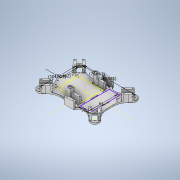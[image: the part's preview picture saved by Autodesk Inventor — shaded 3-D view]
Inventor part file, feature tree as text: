
AUTODESK INVENTOR PART (.ipt)
format: ipt  version: 2020.3 (Build 243373000, 373)  size: 1,453,056 bytes
history: native  units: mm
features: sketch x9, extrude x9, fillet x8, hole x7, projected_geometry x2, plane x1
ambient origin geometry x8: Origin, YZ Plane, XZ Plane, XY Plane, X Axis, Y Axis, Z Axis, Center Point
bodies: Body1 (feature_tree)
feature tree (36):
  sketch  "Sketch1"  dims[d0=135.0deg d4=24.6mm]
  extrude  "Extrusion10"  Depth=24.6mm
  extrude  "Extrusion11"  Depth=70.0mm
  extrude  "Extrusion12"  Depth=8.7mm
  sketch  "Sketch12"  dims[d53=1.5mm d54=20.0mm d59=1.0mm d60=90.0mm d61=135.0deg d70=135.0deg d82=0.7mm d83=0.7mm d84=0.7mm d85=0.7mm d86=6.0mm d87=5.0mm d88=0.0mm d89=20.92mm d90=0.0mm d91=1.9mm d92=6.0mm d93=4.2mm d94=2.0mm d95=90.0deg d96=8.0mm d97=0.0mm d98=2.0mm d99=1.0mm d100=2.0mm d101=0.5mm d103=0.5mm d104=0.5mm d105=18.0mm d108=3.0mm d110=2.9mm d111=6.0mm d112=4.0mm d113=2.0mm d114=90.0deg d115=4.3mm d116=0.0mm d117=30.0mm d119=84.0mm d120=1.9mm d121=6.0mm d122=4.0mm d123=2.0mm d124=90.0deg d125=8.0mm d126=0.0mm d128=12.0mm d129=2.094395mm d130=6.0mm d134=32.32mm d135=0.0mm d136=0.3mm d137=5.6mm d138=6.0mm d139=9.0mm d140=1.1mm d141=90.0deg d142=6.6mm d143=0.0mm d144=0.2mm d145=1.0mm d146=1.5mm d147=10.0mm d148=0.0mm d149=0.0mm d150=1.0mm d151=10.0mm d152=1.5mm d153=10.0mm d154=0.0mm d155=1.0mm d156=10.0mm d158=1.5mm d159=10.0mm d160=0.0mm d161=1.0mm d162=10.0mm d163=1.5mm d164=10.0mm d165=0.0mm d166=2.0mm d173=0.5mm d174=4.0mm d175=1.0mm d176=3.0mm d177=0.5mm d178=9.7mm d179=4.0mm d181=0.2mm d182=6.0mm d183=4.0mm d185=21.842mm d186=0.0mm d187=0.3mm d188=24.0mm d189=52.462385mm d190=74.962385mm d191=2.0mm d192=2.0mm d193=2.0mm d194=2.1mm d195=6.0mm d196=4.0mm d197=2.0mm d198=90.0deg d199=7.3mm d200=0.0mm d201=10.0mm d204=30.0deg d205=25.0mm d206=5.0mm d207=0.0mm d210=15.0mm d211=10.0mm d213=15.0mm d214=4.0mm d215=22.856406mm d216=3.0mm d217=45.0mm d218=3.0mm d219=6.0mm d220=6.5mm d221=2.0mm d222=90.0deg d223=8.0mm d224=20.594885mm d225=3.0mm d226=6.0mm d227=6.5mm d228=2.0mm d229=90.0deg d230=8.0mm d231=20.594885mm d232=149.924769mm d233=104.924769mm]
  extrude  "Extrusion19"  Depth=6.0mm
  hole  "Hole1"  [1 undecoded]
  fillet  "Fillet8"  Radius=20.0mm
  fillet  "Fillet9"  Radius=6.0mm
  fillet  "Fillet11"  Radius=135.0mm
  fillet  "Fillet12"  Radius=15.0mm
  fillet  "Fillet14"  Radius=4.0mm
  sketch  "Sketch2"  dims[d5=12.4mm d6=70.0mm]
  hole  "Hole2"  [1 undecoded]
  sketch  "Sketch3"  dims[d7=60.0mm d9=8.7mm]
  hole  "Hole3"  [1 undecoded]
  fillet  "Fillet13"  Radius=84.0mm
  extrude  "Extrusion13"  Depth=3.0mm
  extrude  "Extrusion14"  Depth=10.0mm
  extrude  "Extrusion15"  Depth=10.0mm
  extrude  "Extrusion16"  Depth=10.0mm
  plane  "Work Plane1"
  hole  "Hole4"  [1 undecoded]
  extrude  "Extrusion18"  TaperAngle=135.0deg  [1 undecoded]
  fillet  "Fillet15"  Radius=0.7mm
  fillet  "Fillet16"  Radius=0.7mm
  hole  "Hole5"  [1 undecoded]
  sketch  "Sketch11"  dims[d51=3.0mm d52=3.0mm]
  hole  "Hole6"  [1 undecoded]
  hole  "Hole7"  [1 undecoded]
  sketch  "Sketch4"  dims[d10=135.0deg d12=6.0mm]
  sketch  "Sketch6"  dims[d13=2.0mm d14=2.0mm d16=20.0mm d23=6.0mm d29=135.0mm d32=15.0mm d33=4.0mm]
  projected_geometry  "Projected Loop1"
  sketch  "Sketch8"  dims[d34=28.4mm d38=4.0mm]
  sketch  "Sketch10"  dims[d40=6.8mm d49=30.0mm d50=84.0mm]
  projected_geometry  "Project Cut Edges4"
note: 8 required parameter values undecoded (feature->parameter linkage not recoverable at this tier; creation-order binding heuristic only, values carry confidence <= 0.55)
